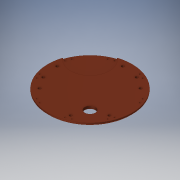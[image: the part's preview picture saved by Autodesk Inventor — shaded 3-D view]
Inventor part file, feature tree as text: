
AUTODESK INVENTOR PART (.ipt)
format: ipt  version: 2018 (Build 220112000, 112)  size: 199,168 bytes
history: native  units: in
note: dims shown in document units (in); Inventor stores cm internally (conversion verified against a paired STEP export)
features: sketch x7, extrude x4, hole x3, pattern_circular x1
ambient origin geometry x8: Origin, YZ Plane, XZ Plane, XY Plane, X Axis, Y Axis, Z Axis, Center Point
bodies: Solid1 (feature_tree)
feature tree (15):
  extrude  "Extrusion1"  Depth=0.25in TaperAngle=0.0deg
  hole  "Hole2"  [1 undecoded]
  pattern_circular  "Circular Pattern2"  Count=8 Angle=360.0deg
  extrude  "Extrusion4"  Depth=4.0in
  sketch  "Sketch8"  dims[d31=7.75in d33=0.0in d34=0.125in d39=4.0in]
  hole  "Hole3"  [1 undecoded]
  extrude  "Extrusion6"  Depth=0.25in
  hole  "Hole4"  [1 undecoded]
  sketch  "Sketch1"  dims[d0=8.0in d1=0.25in d2=0.0in]
  sketch  "Sketch3"  dims[d14=3.75in d15=22.5deg]
  sketch  "Sketch6"  dims[d17=90.0deg]
  sketch  "Sketch7"  dims[d18=0.15in d19=0.224in d20=0.225in d21=0.25in d22=0.5635in d23=0.349in d24=0.8108in d25=3.1496in d26=360.0deg]
  sketch  "Sketch9"  dims[d40=45.0deg d41=1.5in d42=1.0in d43=1.0in d44=0.0in d45=2.5in d46=3.81in d47=135.0deg d48=11.0in d49=5.5in d50=1.9354in d56=6.6in d57=0.266in d58=0.75in d59=0.507in d60=0.25in d61=0.5635in d62=1.0in d63=0.8108in d64=5.85in d65=135.0deg d66=3.7in d69=0.1in d70=0.0in d71=6.8in d72=22.5deg d76=135.0deg d78=0.266in d79=0.75in d80=0.507in d81=0.25in d82=0.5635in d83=1.0in d84=0.8108in d86=0.3108in d88=0.6503in d101=67.5deg]
  sketch  "Sketch5"  dims[d16=0.25in]
  extrude  "Extrusion3"  Depth=0.25in
note: 3 required parameter values undecoded (feature->parameter linkage not recoverable at this tier; creation-order binding heuristic only, values carry confidence <= 0.55)
